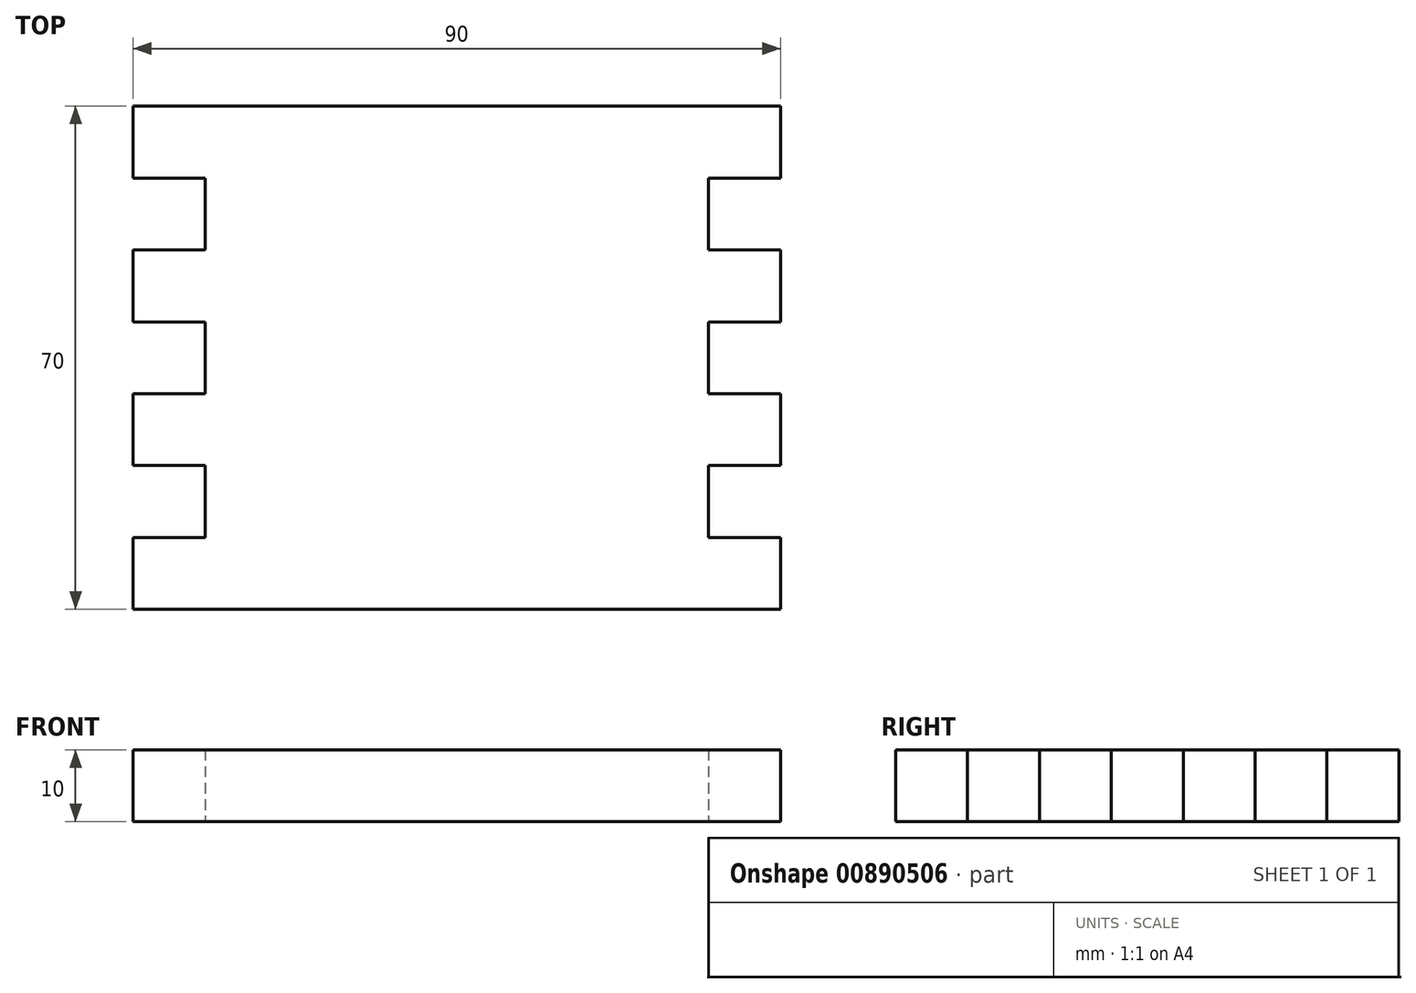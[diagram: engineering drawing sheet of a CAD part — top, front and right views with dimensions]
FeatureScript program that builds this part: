
annotation { "Feature Type Name" : "Feature", "Feature Type Description" : "" }
export const myFeature = defineFeature(function(context is Context, id is Id, definition is map)
    precondition{}
    {
        {
            var Q0;
            Q0=qCreatedBy(makeId("Top.planeOp"),FACE);
            var sketch = newSketch(context, id + "F0", { "sketchPlane" : qUnion([Q0])});
            skLineSegment(sketch, "E0.top", {"start": v(45, -45) * mm, "end": v(0, -45) * mm});
            skPoint(sketch, "E0.middle", {"position": v(0, 0) * mm});
            skLineSegment(sketch, "E1", {"start": v(35, 25) * mm, "end": v(45, 25) * mm});
            skLineSegment(sketch, "E2", {"start": v(45, 25) * mm, "end": v(35, 25) * mm});
            skLineSegment(sketch, "E3", {"start": v(45, 25) * mm, "end": v(45, 15) * mm});
            skLineSegment(sketch, "E4", {"start": v(45, 15) * mm, "end": v(35, 15) * mm});
            skLineSegment(sketch, "E5", {"start": v(35, 15) * mm, "end": v(35, 5) * mm});
            skLineSegment(sketch, "E6", {"start": v(35, 5) * mm, "end": v(45, 5) * mm});
            skLineSegment(sketch, "E7", {"start": v(45, 5) * mm, "end": v(45, -5) * mm});
            skLineSegment(sketch, "E8", {"start": v(45, -5) * mm, "end": v(35, -5) * mm});
            skLineSegment(sketch, "E9", {"start": v(35, -5) * mm, "end": v(35, -15) * mm});
            skLineSegment(sketch, "E10", {"start": v(35, -15) * mm, "end": v(45, -15) * mm});
            skLineSegment(sketch, "E11", {"start": v(45, -15) * mm, "end": v(45, -25) * mm});
            skLineSegment(sketch, "E12", {"start": v(45, -25) * mm, "end": v(35, -25) * mm});
            skLineSegment(sketch, "E13", {"start": v(35, -25) * mm, "end": v(35, -35) * mm});
            skLineSegment(sketch, "E14", {"start": v(35, -35) * mm, "end": v(45, -35) * mm});
            skPoint(sketch, "E15.orphan", {"position": v(-45, 45) * mm});
            skPoint(sketch, "E16.orphan", {"position": v(-45, -45) * mm});
            skLineSegment(sketch, "E17.MirrorCS", {"start": v(-35, 25) * mm, "end": v(-45, 25) * mm});
            skLineSegment(sketch, "E18.MirrorCS", {"start": v(-45, -45) * mm, "end": v(0, -45) * mm});
            skLineSegment(sketch, "E19.MirrorCS", {"start": v(-45, 15) * mm, "end": v(-35, 15) * mm});
            skLineSegment(sketch, "E20.MirrorCS", {"start": v(-35, -15) * mm, "end": v(-45, -15) * mm});
            skLineSegment(sketch, "E21.MirrorCS", {"start": v(-45, -15) * mm, "end": v(-45, -25) * mm});
            skLineSegment(sketch, "E22.MirrorCS", {"start": v(-35, -5) * mm, "end": v(-35, -15) * mm});
            skLineSegment(sketch, "E23.MirrorCS", {"start": v(-45, 25) * mm, "end": v(-35, 25) * mm});
            skLineSegment(sketch, "E24.MirrorCS", {"start": v(-35, -25) * mm, "end": v(-35, -35) * mm});
            skLineSegment(sketch, "E25.MirrorCS", {"start": v(-45, -5) * mm, "end": v(-35, -5) * mm});
            skLineSegment(sketch, "E26.MirrorCS", {"start": v(-35, 5) * mm, "end": v(-45, 5) * mm});
            skLineSegment(sketch, "E27.MirrorCS", {"start": v(-45, 5) * mm, "end": v(-45, -5) * mm});
            skLineSegment(sketch, "E28.MirrorCS", {"start": v(-35, -35) * mm, "end": v(-45, -35) * mm});
            skLineSegment(sketch, "E29.MirrorCS", {"start": v(-45, 25) * mm, "end": v(-45, 15) * mm});
            skLineSegment(sketch, "E30.MirrorCS", {"start": v(-45, -25) * mm, "end": v(-35, -25) * mm});
            skLineSegment(sketch, "E31.MirrorCS", {"start": v(-35, 15) * mm, "end": v(-35, 5) * mm});
            skLineSegment(sketch, "E32.trimOffspring", {"start": v(-45, -35) * mm, "end": v(-45, -45) * mm});
            skLineSegment(sketch, "E33.trimOffspring", {"start": v(45, -35) * mm, "end": v(45, -45) * mm});
            skLineSegment(sketch, "E34", {"start": v(-35, 25) * mm, "end": v(35, 25) * mm});
            skPoint(sketch, "E35.orphan", {"position": v(0, 45) * mm});
            skPoint(sketch, "E0.bottom.start.orphan", {"position": v(45, 45) * mm});
            skPoint(sketch, "E36.end.orphan", {"position": v(45, 35) * mm});
            skPoint(sketch, "E36.start.orphan", {"position": v(35, 35) * mm});
            skSolve(sketch);
        }
        {
            var Q0;
            Q0=makeQuery(id+"F0.imprint","IMPRINT",FACE,{"disambiguationData":[TD([[makeQuery(id+"F0.imprint","IMPRINT",EDGE,{"derivedFrom":sQuery(id+"F0.wireOp",EDGE,"E0.top")}),-1.0]])]});
            extrude(context, id + "F1", {"entities" : qUnion([Q0]), "depth" : 10 * mm, "offsetDistance" : 25 * mm});
        }
    });
